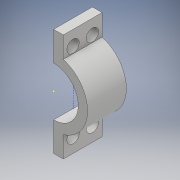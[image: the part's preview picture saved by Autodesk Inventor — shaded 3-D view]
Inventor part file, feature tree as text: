
AUTODESK INVENTOR PART (.ipt)
format: ipt  version: 2018 (Build 220112000, 112)  size: 288,256 bytes
history: native  units: mm
features: sketch x5, extrude x4
ambient origin geometry x8: Origin, YZ Plane, XZ Plane, XY Plane, X Axis, Y Axis, Z Axis, Center Point
bodies: Solid1 (feature_tree)
feature tree (9):
  extrude  "Extrusion1"  Depth=35.0mm
  extrude  "Extrusion2"  Depth=20.0mm TaperAngle=0.0deg
  sketch  "Sketch3"  dims[d6=15.0mm d7=15.0mm]
  sketch  "Sketch4"  dims[d8=5.0mm d9=0.0mm d10=6.35mm]
  extrude  "Extrusion3"  Depth=15.0mm
  extrude  "Extrusion4"  Depth=5.0mm
  sketch  "Sketch1"  dims[d0=25.4mm d1=35.0mm]
  sketch  "Sketch2"  dims[d2=20.0mm d3=0.0mm d4=20.0mm d5=0.0mm]
  sketch  "Sketch5"  dims[d11=6.35mm d12=6.35mm d13=6.35mm d14=6.35mm d15=5.0mm d16=0.0mm]
